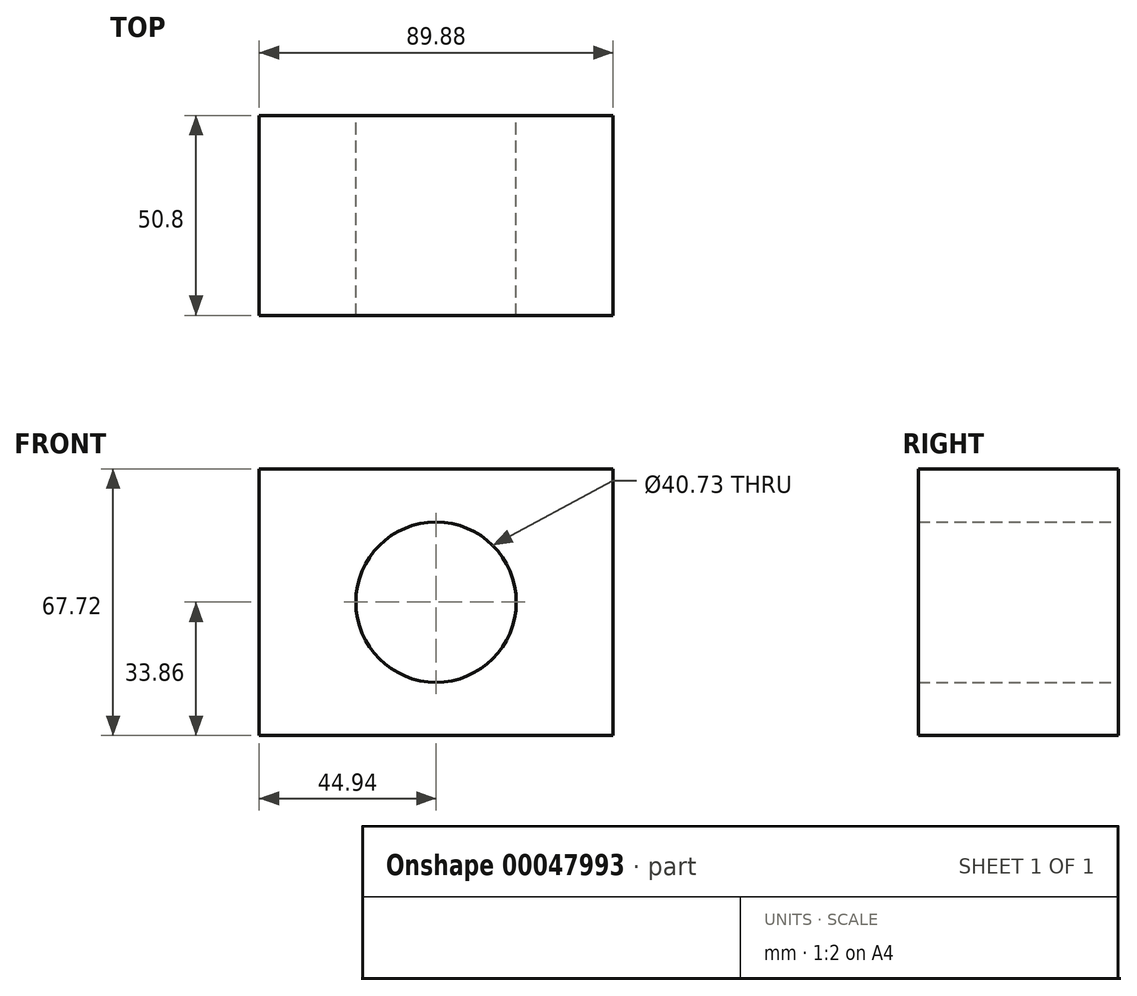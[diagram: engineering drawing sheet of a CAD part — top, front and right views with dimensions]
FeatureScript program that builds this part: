
annotation { "Feature Type Name" : "Feature", "Feature Type Description" : "" }
export const myFeature = defineFeature(function(context is Context, id is Id, definition is map)
    precondition{}
    {
        {
            var Q0;
            Q0=qCreatedBy(makeId("Front.planeOp"),FACE);
            var sketch = newSketch(context, id + "F0", { "sketchPlane" : qUnion([Q0])});
            skLineSegment(sketch, "E0.rect.bottom", {"start": v(44.94, -33.86) * mm, "end": v(-44.94, -33.86) * mm});
            skLineSegment(sketch, "E0.rect.top", {"start": v(44.94, 33.86) * mm, "end": v(-44.94, 33.86) * mm});
            skLineSegment(sketch, "E0.rect.left", {"start": v(44.94, -33.86) * mm, "end": v(44.94, 33.86) * mm});
            skLineSegment(sketch, "E0.rect.right", {"start": v(-44.94, -33.86) * mm, "end": v(-44.94, 33.86) * mm});
            skPoint(sketch, "E0.rect.middle", {"position": v(0, 0) * mm});
            skCircle(sketch, "E1", {"center": v(0, 0) * mm, "radius": 20.36 * mm});
            skSolve(sketch);
        }
        {
            var Q0;
            Q0 = qSketchRegion(id + "F0", true);
            extrude(context, id + "F1", {"entities" : qUnion([Q0]), "depth" : 50.8 * mm});
        }
    });
